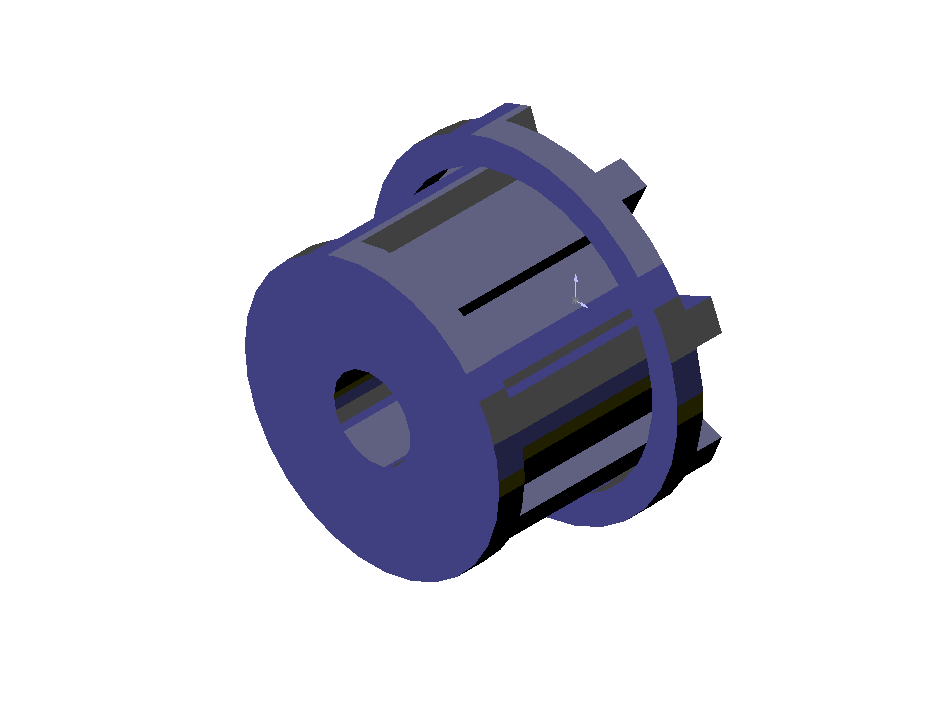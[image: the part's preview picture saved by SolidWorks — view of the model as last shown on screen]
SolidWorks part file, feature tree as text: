
SOLIDWORKS PART (.sldprt)
format: sldprt  version: not decoded by parser v0  size: 133,632 bytes
history: native  units: mm
features: sketch x4, plane x3, extrude x2, cut_extrude x2, material x1, pattern_circular x1 (+10 scaffold rows collapsed)
feature tree (23):
  scaffold x10  (default folders/planes/origin — collapsed)
  material  "Matériau <non spécifié>"
  plane  "Plan1"
  plane  "Plan2"
  plane  "Plan3"
  sketch  "Esquisse1"  dims[D1=3.0mm D2=10.0mm]
  extrude  "Base-Extrusion"  Depth=8mm
  sketch  "Esquisse2"  dims[D1=12.0mm]
  extrude  "Boss.-Extru.1"  Depth=2mm
  sketch  "Esquisse3"  dims[c1.D1=8.5mm c1.D2=0.75mm c2.D2=40.0deg]
  cut_extrude  "Enlèv. mat.-Extru.1"  Depth=1mm
  sketch  "Esquisse4"
  cut_extrude  "Enlèv. mat.-Extru.2"  Depth=1mm
  pattern_circular  "Répétition circulaire1"  Count=8 Angle=45deg
decode coverage: 8 of 9 modeling features carry decoded parameters
note: suppression state not decoded; provenance and decode notes live in map.json
